# Revit family: ASH_ArmitageShanks_WCSeats_Contour21_Splash355SeatOnly
name_source: partatom
category: Plumbing Fixtures
revit_build: Autodesk Revit MEP 2012 (Build: 20110309_2315(x64)
units: mm (PartAtom-declared; Revit-internal decimal feet)

## types (4) — shared parameters
Accessories = www.idealspec.co.uk
AreaUnits = millimeters
Assembly Code = C1030200
AssetType = Fixed
Brand = Armitage Shanks
ConnectionType = Mechanical
Default Elevation = 1219 mm
DurationUnit = year
ECA = No
ExpectedLife = 15
Features = Seat ring only for 355 mm bowls
Help = www.idealspec.co.uk/contact-us.html
IfcExportAs = IfcSanitaryTerminalType
IfcExportType = WCSEAT
InstallationInstructions = www.idealspec.co.uk/resources.html
LinearUnits = millimeters
ManufacturerURL = www.idealspec.co.uk
Material = Plastic
NBSDescription = WC seats and covers
NBSReference = 45-35-70/391
NettWeight = 1.2 Kg
NominalDepth = 441 mm
NominalHeight = 58 mm  [stored 0.190289 ft]
NominalLength = 441 mm
NominalWidth = 375 mm
SeatColor = White
SeatHasCover = No
SeatMaterial = Plastic
SeatType = RingSeat
Shape = Sculptured
Size = 375 x 441x 58mm
Space = Internal
SpareParts = www.fastpart-spares.co.uk
URL = www.idealspec.co.uk
Uniclass2 = Pr_40_20_93_95
Version = 2
VolumeUnits = Litres
WRAS = No
WarrantyDescription = Manufacturers Warranty
WarrantyDurationParts = 5
WarrantyDurationUnit = year
WaterEfficientProduct = No
zero-valued in all types: CWFU, Cost, HWFU, WFU

## per-type parameters (varying)
| type | BIMObjectName | Color | Description | Finish | Model | ModelNumber | ModelReference | Name | ProductInformation | SeatSKU |
| S454501-Contour 21 Splash seat ring only for 355mm bowls-White | ASH_ArmitageShanks_WCSeats_Contour21Splash_S4536 | White | Contour 21 splash seat and cover for 355 mm bowls | White | S453601 | S453601 | Contour 21 splash seat and cover for 355 mm bowls | WCSeats_Contour21Splash-S4536_ArmitageShanks | www.idealspec.co.uk/assets/datasheet/S454501 | ASH_ArmitageShanks _WC_White1_Render |
| S454536-Contour 21 Splash seat ring only for 355mm bowls- Blue | ASH_ArmitageShanks_WCSeats_Contour21Splash_S4545 | Blue | Contour 21 splash seat and cover for 355 mm bowls | Blue | S454536 | S454536 | Contour 21 splash seat and cover for 355 mm bowls | WCSeats_Contour21Splash-S4545_ArmitageShanks | www.idealspec.co.uk/assets/datasheet/S454536 | ASH_ArmitageShanks _WC_Blue_Render |
| S454579-Contour 21 Splash seat ring only for 355mm bowls-Yellow | ASH_ArmitageShanks_WCSeats_Contour21Splash_S4545 | Yellow | Contour 21 splash seat ring only for 355 mm bowls | Yellow | S454579 | S454579 | Contour 21 splash seat ring only for 355 mm bowls | WCSeats_Contour21Splash-S4545_ArmitageShanks | www.idealspec.co.uk/assets/datasheet/S454579 | ASH_ArmitageShanks _WCSeat_Yellow_Render |
| S4545GQ-Contour 21 Splash seat ring only for 355mm bowls-Red | ASH_ArmitageShanks_WCSeats_Contour21Splash_S4545 | Red | Contour 21 splash seat and cover for 355 mm bowls | Red | S4545GQ | S4545GQ | Contour 21 splash seat and cover for 355 mm bowls | WCSeats_Contour21Splash-S4545_ArmitageShanks | www.idealspec.co.uk/assets/datasheet/S4545GQ | ASH_ArmitageShanks _WC_Red_Render |

note: [stored X ft] marks values corroborated as IEEE doubles in the binary element streams (Revit-internal decimal feet)
